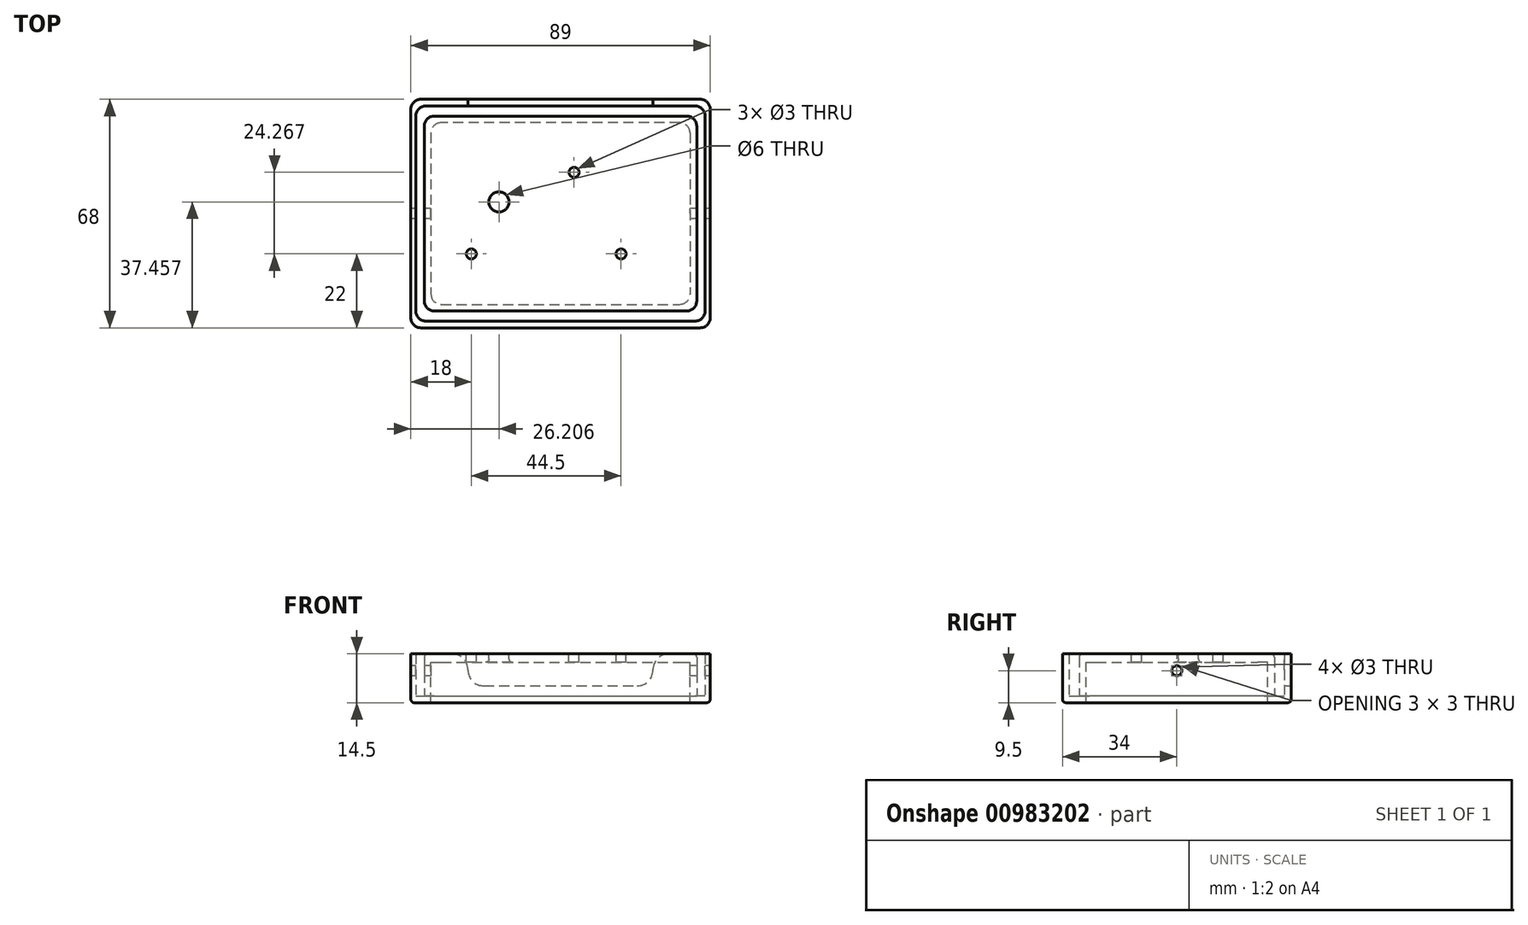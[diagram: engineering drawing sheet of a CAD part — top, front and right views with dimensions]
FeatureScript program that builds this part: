
annotation { "Feature Type Name" : "Feature", "Feature Type Description" : "" }
export const myFeature = defineFeature(function(context is Context, id is Id, definition is map)
    precondition{}
    {
        {
            var Q0;
            Q0=qCreatedBy(makeId("Top.planeOp"),FACE);
            var sketch = newSketch(context, id + "F0", { "sketchPlane" : qUnion([Q0])});
            skLineSegment(sketch, "E0.bottom", {"start": v(40.5, -29) * mm, "end": v(-40.5, -29) * mm});
            skLineSegment(sketch, "E0.top", {"start": v(40.5, 29) * mm, "end": v(-40.5, 29) * mm});
            skLineSegment(sketch, "E0.left", {"start": v(40.5, -29) * mm, "end": v(40.5, 29) * mm});
            skLineSegment(sketch, "E0.right", {"start": v(-40.5, -29) * mm, "end": v(-40.5, 29) * mm});
            skPoint(sketch, "E0.middle", {"position": v(0, 0) * mm});
            skSolve(sketch);
        }
        {
            var Q0;
            Q0 = qSketchRegion(id + "F0", true);
            extrude(context, id + "F1", {"entities" : qUnion([Q0]), "depth" : 2.5 * mm, "offsetDistance" : 25 * mm});
        }
        {
            var Q0;
            Q0=makeQuery(id+"F1.opExtrude","CAP_FACE",FACE,{"disambiguationData":[OSD([sQuery(id+"F0.wireOp",EDGE,"E0.bottom"),sQuery(id+"F0.wireOp",EDGE,"E0.top"),sQuery(id+"F0.wireOp",EDGE,"E0.left"),sQuery(id+"F0.wireOp",EDGE,"E0.right")])],"isStart":false});
            var sketch = newSketch(context, id + "F2", { "sketchPlane" : qUnion([Q0])});
            skCircle(sketch, "E1", {"center": v(-26.5, -12) * mm, "radius": 1.5 * mm});
            skCircle(sketch, "E2", {"center": v(18, -12) * mm, "radius": 1.5 * mm});
            skCircle(sketch, "E3", {"center": v(4.03, 12.27) * mm, "radius": 1.5 * mm});
            skCircle(sketch, "E4", {"center": v(-18.3, 3.46) * mm, "radius": 3 * mm});
            skSolve(sketch);
        }
        {
            var Q0;
            Q0 = qSketchRegion(id + "F2", true);
            extrude(context, id + "F3", {"entities" : qUnion([Q0]), "operationType" : NewBodyOperationType.REMOVE, "oppositeDirection" : true, "depth" : 25 * mm, "offsetDistance" : 25 * mm});
        }
        {
            var Q0;
            Q0=makeQuery(id+"F1.opExtrude","CAP_FACE",FACE,{"disambiguationData":[OSD([sQuery(id+"F0.wireOp",EDGE,"E0.bottom"),sQuery(id+"F0.wireOp",EDGE,"E0.top"),sQuery(id+"F0.wireOp",EDGE,"E0.left"),sQuery(id+"F0.wireOp",EDGE,"E0.right")])],"isStart":true});
            var sketch = newSketch(context, id + "F4", { "sketchPlane" : qUnion([Q0])});
            skLineSegment(sketch, "E5.bottom", {"start": v(-40.5, 29) * mm, "end": v(40.5, 29) * mm});
            skLineSegment(sketch, "E5.top", {"start": v(-40.5, 27) * mm, "end": v(40.5, 27) * mm});
            skLineSegment(sketch, "E5.left", {"start": v(-40.5, 29) * mm, "end": v(-40.5, 27) * mm});
            skLineSegment(sketch, "E5.right", {"start": v(40.5, 29) * mm, "end": v(40.5, 27) * mm});
            skLineSegment(sketch, "E6.bottom", {"start": v(40.5, -29) * mm, "end": v(-40.5, -29) * mm});
            skLineSegment(sketch, "E6.top", {"start": v(40.5, -27) * mm, "end": v(-40.5, -27) * mm});
            skLineSegment(sketch, "E6.left", {"start": v(40.5, -29) * mm, "end": v(40.5, -27) * mm});
            skLineSegment(sketch, "E6.right", {"start": v(-40.5, -29) * mm, "end": v(-40.5, -27) * mm});
            skLineSegment(sketch, "E7.bottom", {"start": v(-40.5, -29) * mm, "end": v(-38.5, -29) * mm});
            skLineSegment(sketch, "E7.top", {"start": v(-40.5, 29) * mm, "end": v(-38.5, 29) * mm});
            skLineSegment(sketch, "E7.left", {"start": v(-40.5, -29) * mm, "end": v(-40.5, 29) * mm});
            skLineSegment(sketch, "E7.right", {"start": v(-38.5, -29) * mm, "end": v(-38.5, 29) * mm});
            skLineSegment(sketch, "E8.bottom", {"start": v(40.5, 29) * mm, "end": v(38.5, 29) * mm});
            skLineSegment(sketch, "E8.top", {"start": v(40.5, -29) * mm, "end": v(38.5, -29) * mm});
            skLineSegment(sketch, "E8.left", {"start": v(40.5, 29) * mm, "end": v(40.5, -29) * mm});
            skLineSegment(sketch, "E8.right", {"start": v(38.5, 29) * mm, "end": v(38.5, -29) * mm});
            skSolve(sketch);
        }
        {
            var Q0;
            Q0 = qSketchRegion(id + "F4", true);
            extrude(context, id + "F5", {"entities" : qUnion([Q0]), "operationType" : NewBodyOperationType.ADD, "depth" : 12 * mm, "offsetDistance" : 25 * mm});
        }
        {
            var Q0;
            Q0=makeQuery(id+"F5.boolean.opBoolean","MERGE",FACE,{"derivedFrom":[makeQuery(id+"F1.opExtrude","SWEPT_FACE",FACE,{"disambiguationData":[OSD([sQuery(id+"F0.wireOp",EDGE,"E0.bottom")])]}),makeQuery(id+"F5.opExtrude","SWEPT_FACE",FACE,{"disambiguationData":[OSD([sQuery(id+"F4.wireOp",EDGE,"E5.bottom"),sQuery(id+"F4.wireOp",EDGE,"E7.top"),sQuery(id+"F4.wireOp",EDGE,"E8.bottom")])]})]});
            var sketch = newSketch(context, id + "F6", { "sketchPlane" : qUnion([Q0])});
            skLineSegment(sketch, "E9.bottom", {"start": v(44.5, -12) * mm, "end": v(-44.5, -12) * mm});
            skLineSegment(sketch, "E9.top", {"start": v(44.5, -10) * mm, "end": v(-44.5, -10) * mm});
            skLineSegment(sketch, "E9.left", {"start": v(44.5, -12) * mm, "end": v(44.5, -10) * mm});
            skLineSegment(sketch, "E9.right", {"start": v(-44.5, -12) * mm, "end": v(-44.5, -10) * mm});
            skPoint(sketch, "E9.middle", {"position": v(0, -11) * mm});
            skSolve(sketch);
        }
        {
            var Q0;
            Q0 = qSketchRegion(id + "F6", true);
            extrude(context, id + "F7", {"entities" : qUnion([Q0]), "operationType" : NewBodyOperationType.ADD, "depth" : 5 * mm, "offsetDistance" : 25 * mm, "hasSecondDirection" : true, "secondDirectionOppositeDirection" : true, "secondDirectionDepth" : 63 * mm});
        }
        {
            var Q0;
            Q0=makeQuery(id+"F7.boolean.opBoolean","MERGE",FACE,{"derivedFrom":[makeQuery(id+"F5.opExtrude","CAP_FACE",FACE,{"disambiguationData":[OSD([sQuery(id+"F4.wireOp",EDGE,"E5.bottom"),sQuery(id+"F4.wireOp",EDGE,"E5.top"),sQuery(id+"F4.wireOp",EDGE,"E6.bottom"),sQuery(id+"F4.wireOp",EDGE,"E6.top"),sQuery(id+"F4.wireOp",EDGE,"E7.bottom"),sQuery(id+"F4.wireOp",EDGE,"E7.top"),sQuery(id+"F4.wireOp",EDGE,"E7.left"),sQuery(id+"F4.wireOp",EDGE,"E7.right"),sQuery(id+"F4.wireOp",EDGE,"E8.bottom"),sQuery(id+"F4.wireOp",EDGE,"E8.top"),sQuery(id+"F4.wireOp",EDGE,"E8.left"),sQuery(id+"F4.wireOp",EDGE,"E8.right")])],"isStart":false}),makeQuery(id+"F7.opExtrude","SWEPT_FACE",FACE,{"disambiguationData":[OSD([sQuery(id+"F6.wireOp",EDGE,"E9.bottom")])]})]});
            var sketch = newSketch(context, id + "F8", { "sketchPlane" : qUnion([Q0])});
            skLineSegment(sketch, "E10.bottom", {"start": v(38.5, -27) * mm, "end": v(-38.5, -27) * mm});
            skLineSegment(sketch, "E10.top", {"start": v(38.5, 27) * mm, "end": v(-38.5, 27) * mm});
            skLineSegment(sketch, "E10.left", {"start": v(38.5, -27) * mm, "end": v(38.5, 27) * mm});
            skLineSegment(sketch, "E10.right", {"start": v(-38.5, -27) * mm, "end": v(-38.5, 27) * mm});
            skPoint(sketch, "E10.middle", {"position": v(0, 0) * mm});
            skSolve(sketch);
        }
        {
            var Q0;
            Q0 = qSketchRegion(id + "F8", true);
            extrude(context, id + "F9", {"entities" : qUnion([Q0]), "operationType" : NewBodyOperationType.REMOVE, "endBound" : BoundingType.UP_TO_NEXT, "oppositeDirection" : true, "depth" : 25 * mm, "offsetDistance" : 25 * mm});
        }
        {
            var Q0;
            {var subQ2=sQuery(id+"F6.wireOp",EDGE,"E9.top");Q0=makeQuery(id+"F7.boolean.opBoolean","SPLIT",FACE,{"disambiguationData":[TD([makeQuery(id+"F1.opExtrude","SWEPT_FACE",FACE,{"disambiguationData":[OSD([sQuery(id+"F0.wireOp",EDGE,"E0.bottom")])]})])],"derivedFrom":makeQuery(id+"F7.opExtrude","SWEPT_FACE",FACE,{"disambiguationData":[OSD([subQ2])]})});}
            var sketch = newSketch(context, id + "F10", { "sketchPlane" : qUnion([Q0])});
            skLineSegment(sketch, "E11.bottom", {"start": v(-44.5, -34) * mm, "end": v(44.5, -34) * mm});
            skLineSegment(sketch, "E11.top", {"start": v(-44.5, -32) * mm, "end": v(44.5, -32) * mm});
            skLineSegment(sketch, "E11.left", {"start": v(-44.5, -34) * mm, "end": v(-44.5, -32) * mm});
            skLineSegment(sketch, "E11.right", {"start": v(44.5, -34) * mm, "end": v(44.5, -32) * mm});
            skLineSegment(sketch, "E12.bottom", {"start": v(-44.5, 34) * mm, "end": v(44.5, 34) * mm});
            skLineSegment(sketch, "E12.top", {"start": v(-44.5, 32) * mm, "end": v(44.5, 32) * mm});
            skLineSegment(sketch, "E12.left", {"start": v(-44.5, 34) * mm, "end": v(-44.5, 32) * mm});
            skLineSegment(sketch, "E12.right", {"start": v(44.5, 34) * mm, "end": v(44.5, 32) * mm});
            skLineSegment(sketch, "E13.bottom", {"start": v(-44.5, 34) * mm, "end": v(-43, 34) * mm});
            skLineSegment(sketch, "E13.top", {"start": v(-44.5, -34) * mm, "end": v(-43, -34) * mm});
            skLineSegment(sketch, "E13.left", {"start": v(-44.5, 34) * mm, "end": v(-44.5, -34) * mm});
            skLineSegment(sketch, "E13.right", {"start": v(-43, 34) * mm, "end": v(-43, -34) * mm});
            skLineSegment(sketch, "E14.bottom", {"start": v(44.5, 34) * mm, "end": v(43, 34) * mm});
            skLineSegment(sketch, "E14.top", {"start": v(44.5, -34) * mm, "end": v(43, -34) * mm});
            skLineSegment(sketch, "E14.left", {"start": v(44.5, 34) * mm, "end": v(44.5, -34) * mm});
            skLineSegment(sketch, "E14.right", {"start": v(43, 34) * mm, "end": v(43, -34) * mm});
            skSolve(sketch);
        }
        {
            var Q0;
            Q0 = qSketchRegion(id + "F10", true);
            extrude(context, id + "F11", {"entities" : qUnion([Q0]), "operationType" : NewBodyOperationType.ADD, "depth" : 12.5 * mm, "offsetDistance" : 25 * mm});
        }
        {
            var Q0;
            Q0=makeQuery(id+"F11.boolean.opBoolean","MERGE",FACE,{"derivedFrom":[makeQuery(id+"F7.opExtrude","CAP_FACE",FACE,{"disambiguationData":[OSD([sQuery(id+"F6.wireOp",EDGE,"E9.bottom"),sQuery(id+"F6.wireOp",EDGE,"E9.top"),sQuery(id+"F6.wireOp",EDGE,"E9.left"),sQuery(id+"F6.wireOp",EDGE,"E9.right")])],"isStart":true}),makeQuery(id+"F11.opExtrude","SWEPT_FACE",FACE,{"disambiguationData":[OSD([sQuery(id+"F10.wireOp",EDGE,"E12.bottom"),sQuery(id+"F10.wireOp",EDGE,"E13.bottom"),sQuery(id+"F10.wireOp",EDGE,"E14.bottom")])]})]});
            var sketch = newSketch(context, id + "F12", { "sketchPlane" : qUnion([Q0])});
            skLineSegment(sketch, "E15.bottom", {"start": v(27.5, -7) * mm, "end": v(-27.5, -7) * mm});
            skLineSegment(sketch, "E15.top", {"start": v(27.5, 7) * mm, "end": v(-27.5, 7) * mm});
            skLineSegment(sketch, "E15.left", {"start": v(27.5, -7) * mm, "end": v(27.5, 7) * mm});
            skLineSegment(sketch, "E15.right", {"start": v(-27.5, -7) * mm, "end": v(-27.5, 7) * mm});
            skPoint(sketch, "E15.middle", {"position": v(0, 0) * mm});
            skSolve(sketch);
        }
        {
            var Q0;
            Q0 = qSketchRegion(id + "F12", true);
            extrude(context, id + "F13", {"entities" : qUnion([Q0]), "operationType" : NewBodyOperationType.REMOVE, "oppositeDirection" : true, "depth" : 2 * mm, "offsetDistance" : 25 * mm});
        }
        {
            var Q0;
            Q0=makeQuery(id+"F13.boolean.opBoolean","COPY",EDGE,{"derivedFrom":makeQuery(id+"F13.opExtrude","SWEPT_EDGE",EDGE,{"disambiguationData":[OSD([sQuery(id+"F12.wireOp",EDGE,"E15.bottom"),sQuery(id+"F12.wireOp",EDGE,"E15.right")])]})});
            var Q1;
            Q1=makeQuery(id+"F13.boolean.opBoolean","COPY",EDGE,{"derivedFrom":makeQuery(id+"F13.opExtrude","SWEPT_EDGE",EDGE,{"disambiguationData":[OSD([sQuery(id+"F12.wireOp",EDGE,"E15.bottom"),sQuery(id+"F12.wireOp",EDGE,"E15.left")])]})});
            var Q2;
            Q2=makeQuery(id+"F13.boolean.opBoolean","INTERSECT",EDGE,{"derivedFrom":[makeQuery(id+"F11.opExtrude","CAP_FACE",FACE,{"disambiguationData":[OSD([sQuery(id+"F10.wireOp",EDGE,"E11.bottom"),sQuery(id+"F10.wireOp",EDGE,"E11.top"),sQuery(id+"F10.wireOp",EDGE,"E12.bottom"),sQuery(id+"F10.wireOp",EDGE,"E12.top"),sQuery(id+"F10.wireOp",EDGE,"E13.bottom"),sQuery(id+"F10.wireOp",EDGE,"E13.top"),sQuery(id+"F10.wireOp",EDGE,"E13.left"),sQuery(id+"F10.wireOp",EDGE,"E13.right"),sQuery(id+"F10.wireOp",EDGE,"E14.bottom"),sQuery(id+"F10.wireOp",EDGE,"E14.top"),sQuery(id+"F10.wireOp",EDGE,"E14.left"),sQuery(id+"F10.wireOp",EDGE,"E14.right")])],"isStart":false}),makeQuery(id+"F13.opExtrude","SWEPT_FACE",FACE,{"disambiguationData":[OSD([sQuery(id+"F12.wireOp",EDGE,"E15.right")])]})]});
            var Q3;
            Q3=makeQuery(id+"F13.boolean.opBoolean","INTERSECT",EDGE,{"derivedFrom":[makeQuery(id+"F11.opExtrude","CAP_FACE",FACE,{"disambiguationData":[OSD([sQuery(id+"F10.wireOp",EDGE,"E11.bottom"),sQuery(id+"F10.wireOp",EDGE,"E11.top"),sQuery(id+"F10.wireOp",EDGE,"E12.bottom"),sQuery(id+"F10.wireOp",EDGE,"E12.top"),sQuery(id+"F10.wireOp",EDGE,"E13.bottom"),sQuery(id+"F10.wireOp",EDGE,"E13.top"),sQuery(id+"F10.wireOp",EDGE,"E13.left"),sQuery(id+"F10.wireOp",EDGE,"E13.right"),sQuery(id+"F10.wireOp",EDGE,"E14.bottom"),sQuery(id+"F10.wireOp",EDGE,"E14.top"),sQuery(id+"F10.wireOp",EDGE,"E14.left"),sQuery(id+"F10.wireOp",EDGE,"E14.right")])],"isStart":false}),makeQuery(id+"F13.opExtrude","SWEPT_FACE",FACE,{"disambiguationData":[OSD([sQuery(id+"F12.wireOp",EDGE,"E15.left")])]})]});
            fillet(context, id + "F14", {"entities" : qUnion([Q0, Q1, Q2, Q3]), "radius" : 4.7 * mm, "tangentPropagation" : true, "allowEdgeOverflow" : false});
        }
        {
            var Q0;
            Q0=makeQuery(id+"F5.boolean.opBoolean","MERGE",EDGE,{"derivedFrom":[makeQuery(id+"F1.opExtrude","SWEPT_EDGE",EDGE,{"disambiguationData":[OSD([sQuery(id+"F0.wireOp",EDGE,"E0.bottom"),sQuery(id+"F0.wireOp",EDGE,"E0.left")])]}),makeQuery(id+"F5.opExtrude","SWEPT_EDGE",EDGE,{"disambiguationData":[OSD([sQuery(id+"F4.wireOp",EDGE,"E8.bottom"),sQuery(id+"F4.wireOp",EDGE,"E8.left")])]})]});
            var Q1;
            Q1=makeQuery(id+"F5.boolean.opBoolean","MERGE",EDGE,{"derivedFrom":[makeQuery(id+"F1.opExtrude","SWEPT_EDGE",EDGE,{"disambiguationData":[OSD([sQuery(id+"F0.wireOp",EDGE,"E0.bottom"),sQuery(id+"F0.wireOp",EDGE,"E0.right")])]}),makeQuery(id+"F5.opExtrude","SWEPT_EDGE",EDGE,{"disambiguationData":[OSD([sQuery(id+"F4.wireOp",EDGE,"E7.top"),sQuery(id+"F4.wireOp",EDGE,"E7.left")])]})]});
            var Q2;
            Q2=makeQuery(id+"F5.boolean.opBoolean","MERGE",EDGE,{"derivedFrom":[makeQuery(id+"F1.opExtrude","SWEPT_EDGE",EDGE,{"disambiguationData":[OSD([sQuery(id+"F0.wireOp",EDGE,"E0.top"),sQuery(id+"F0.wireOp",EDGE,"E0.left")])]}),makeQuery(id+"F5.opExtrude","SWEPT_EDGE",EDGE,{"disambiguationData":[OSD([sQuery(id+"F4.wireOp",EDGE,"E8.top"),sQuery(id+"F4.wireOp",EDGE,"E8.left")])]})]});
            var Q3;
            Q3=makeQuery(id+"F5.boolean.opBoolean","MERGE",EDGE,{"derivedFrom":[makeQuery(id+"F1.opExtrude","SWEPT_EDGE",EDGE,{"disambiguationData":[OSD([sQuery(id+"F0.wireOp",EDGE,"E0.top"),sQuery(id+"F0.wireOp",EDGE,"E0.right")])]}),makeQuery(id+"F5.opExtrude","SWEPT_EDGE",EDGE,{"disambiguationData":[OSD([sQuery(id+"F4.wireOp",EDGE,"E7.bottom"),sQuery(id+"F4.wireOp",EDGE,"E7.left")])]})]});
            var Q4;
            {var subQ0=sQuery(id+"F4.wireOp",EDGE,"E8.right");var subQ1=sQuery(id+"F4.wireOp",EDGE,"E6.top");Q4=makeQuery(id+"F9.boolean.opBoolean","MERGE",EDGE,{"derivedFrom":[makeQuery(id+"F5.opExtrude","SWEPT_EDGE",EDGE,{"disambiguationData":[OSD([subQ1,subQ0])]})],"fromTools":[makeQuery(id+"F9.opExtrude","SWEPT_EDGE",EDGE,{"disambiguationData":[OSD([subQ1,subQ0,sQuery(id+"F6.wireOp",EDGE,"E9.top")])]})]});}
            var Q5;
            {var subQ0=sQuery(id+"F4.wireOp",EDGE,"E7.right");var subQ1=sQuery(id+"F4.wireOp",EDGE,"E6.top");Q5=makeQuery(id+"F9.boolean.opBoolean","MERGE",EDGE,{"derivedFrom":[makeQuery(id+"F5.opExtrude","SWEPT_EDGE",EDGE,{"disambiguationData":[OSD([subQ1,subQ0])]})],"fromTools":[makeQuery(id+"F9.opExtrude","SWEPT_EDGE",EDGE,{"disambiguationData":[OSD([subQ1,subQ0,sQuery(id+"F6.wireOp",EDGE,"E9.top")])]})]});}
            var Q6;
            {var subQ0=sQuery(id+"F4.wireOp",EDGE,"E7.right");var subQ1=sQuery(id+"F4.wireOp",EDGE,"E5.top");Q6=makeQuery(id+"F9.boolean.opBoolean","MERGE",EDGE,{"derivedFrom":[makeQuery(id+"F5.opExtrude","SWEPT_EDGE",EDGE,{"disambiguationData":[OSD([subQ1,subQ0])]})],"fromTools":[makeQuery(id+"F9.opExtrude","SWEPT_EDGE",EDGE,{"disambiguationData":[OSD([subQ1,subQ0,sQuery(id+"F6.wireOp",EDGE,"E9.top")])]})]});}
            var Q7;
            Q7=makeQuery(id+"F9.boolean.opBoolean","MERGE",EDGE,{"derivedFrom":[makeQuery(id+"F5.opExtrude","SWEPT_EDGE",EDGE,{"disambiguationData":[OSD([sQuery(id+"F4.wireOp",EDGE,"E5.top"),sQuery(id+"F4.wireOp",EDGE,"E8.right")])]})],"fromTools":[makeQuery(id+"F9.opExtrude","SWEPT_EDGE",EDGE,{"disambiguationData":[OSD([sQuery(id+"F8.wireOp",EDGE,"E10.top"),sQuery(id+"F8.wireOp",EDGE,"E10.left")])]})]});
            var Q8;
            Q8=makeQuery(id+"F11.boolean.opBoolean","MERGE",EDGE,{"derivedFrom":[makeQuery(id+"F7.opExtrude","CAP_EDGE",EDGE,{"disambiguationData":[OSD([sQuery(id+"F6.wireOp",EDGE,"E9.left")])],"isStart":true}),makeQuery(id+"F11.opExtrude","SWEPT_EDGE",EDGE,{"disambiguationData":[OSD([sQuery(id+"F10.wireOp",EDGE,"E14.bottom"),sQuery(id+"F10.wireOp",EDGE,"E14.left")])]})]});
            var Q9;
            Q9=makeQuery(id+"F11.boolean.opBoolean","MERGE",EDGE,{"derivedFrom":[makeQuery(id+"F7.opExtrude","CAP_EDGE",EDGE,{"disambiguationData":[OSD([sQuery(id+"F6.wireOp",EDGE,"E9.right")])],"isStart":false}),makeQuery(id+"F11.opExtrude","SWEPT_EDGE",EDGE,{"disambiguationData":[OSD([sQuery(id+"F10.wireOp",EDGE,"E13.top"),sQuery(id+"F10.wireOp",EDGE,"E13.left")])]})]});
            var Q10;
            Q10=makeQuery(id+"F11.boolean.opBoolean","MERGE",EDGE,{"derivedFrom":[makeQuery(id+"F7.opExtrude","CAP_EDGE",EDGE,{"disambiguationData":[OSD([sQuery(id+"F6.wireOp",EDGE,"E9.left")])],"isStart":false}),makeQuery(id+"F11.opExtrude","SWEPT_EDGE",EDGE,{"disambiguationData":[OSD([sQuery(id+"F10.wireOp",EDGE,"E14.top"),sQuery(id+"F10.wireOp",EDGE,"E14.left")])]})]});
            var Q11;
            Q11=makeQuery(id+"F11.boolean.opBoolean","MERGE",EDGE,{"derivedFrom":[makeQuery(id+"F7.opExtrude","CAP_EDGE",EDGE,{"disambiguationData":[OSD([sQuery(id+"F6.wireOp",EDGE,"E9.right")])],"isStart":true}),makeQuery(id+"F11.opExtrude","SWEPT_EDGE",EDGE,{"disambiguationData":[OSD([sQuery(id+"F10.wireOp",EDGE,"E13.bottom"),sQuery(id+"F10.wireOp",EDGE,"E13.left")])]})]});
            fillet(context, id + "F15", {"entities" : qUnion([Q0, Q1, Q2, Q3, Q4, Q5, Q6, Q7, Q8, Q9, Q10, Q11]), "radius" : 3 * mm, "tangentPropagation" : true, "allowEdgeOverflow" : false});
        }
        {
            var Q0;
            Q0=makeQuery(id+"F11.boolean.opBoolean","MERGE",FACE,{"derivedFrom":[makeQuery(id+"F7.opExtrude","SWEPT_FACE",FACE,{"disambiguationData":[OSD([sQuery(id+"F6.wireOp",EDGE,"E9.right")])]}),makeQuery(id+"F11.opExtrude","SWEPT_FACE",FACE,{"disambiguationData":[OSD([sQuery(id+"F10.wireOp",EDGE,"E13.left")])]})]});
            var sketch = newSketch(context, id + "F16", { "sketchPlane" : qUnion([Q0])});
            skCircle(sketch, "E16", {"center": v(0, -2.5) * mm, "radius": 1.5 * mm});
            skSolve(sketch);
        }
        {
            var Q0;
            Q0 = qSketchRegion(id + "F16", true);
            extrude(context, id + "F17", {"entities" : qUnion([Q0]), "operationType" : NewBodyOperationType.REMOVE, "endBound" : BoundingType.THROUGH_ALL, "oppositeDirection" : true, "depth" : 25 * mm, "offsetDistance" : 25 * mm});
        }
        {
            var Q0;
            Q0=makeQuery(id+"F11.opExtrude","SWEPT_EDGE",EDGE,{"disambiguationData":[OSD([sQuery(id+"F10.wireOp",EDGE,"E11.top"),sQuery(id+"F10.wireOp",EDGE,"E14.right")])]});
            var Q1;
            Q1=makeQuery(id+"F11.opExtrude","SWEPT_EDGE",EDGE,{"disambiguationData":[OSD([sQuery(id+"F10.wireOp",EDGE,"E11.top"),sQuery(id+"F10.wireOp",EDGE,"E13.right")])]});
            var Q2;
            Q2=makeQuery(id+"F11.opExtrude","SWEPT_EDGE",EDGE,{"disambiguationData":[OSD([sQuery(id+"F10.wireOp",EDGE,"E12.top"),sQuery(id+"F10.wireOp",EDGE,"E14.right")])]});
            var Q3;
            Q3=makeQuery(id+"F11.opExtrude","SWEPT_EDGE",EDGE,{"disambiguationData":[OSD([sQuery(id+"F10.wireOp",EDGE,"E12.top"),sQuery(id+"F10.wireOp",EDGE,"E13.right")])]});
            fillet(context, id + "F18", {"entities" : qUnion([Q0, Q1, Q2, Q3]), "radius" : 3 * mm, "tangentPropagation" : true, "allowEdgeOverflow" : false});
        }
        {
            var Q0;
            Q0=makeQuery(id+"F1.opExtrude","CAP_EDGE",EDGE,{"disambiguationData":[OSD([sQuery(id+"F0.wireOp",EDGE,"E0.bottom")])],"isStart":false});
            var Q1;
            Q1=makeQuery(id+"F5.opExtrude","CAP_EDGE",EDGE,{"disambiguationData":[OSD([sQuery(id+"F4.wireOp",EDGE,"E6.top")])],"isStart":true});
            var Q2;
            Q2=makeQuery(id+"F9.boolean.opBoolean","COPY",EDGE,{"derivedFrom":makeQuery(id+"F9.opExtrude","CAP_EDGE",EDGE,{"disambiguationData":[OSD([sQuery(id+"F8.wireOp",EDGE,"E10.bottom")])],"isStart":true})});
            var Q3;
            Q3=makeQuery(id+"F7.opExtrude","CAP_EDGE",EDGE,{"disambiguationData":[OSD([sQuery(id+"F6.wireOp",EDGE,"E9.bottom")])],"isStart":true});
            fillet(context, id + "F19", {"entities" : qUnion([Q0, Q1, Q2, Q3]), "radius" : 1 * mm, "tangentPropagation" : true, "allowEdgeOverflow" : false});
        }
        {
            var Q0;
            Q0=makeQuery(id+"F3.boolean.opBoolean","INTERSECT",EDGE,{"derivedFrom":[makeQuery(id+"F1.opExtrude","CAP_FACE",FACE,{"disambiguationData":[OSD([sQuery(id+"F0.wireOp",EDGE,"E0.bottom"),sQuery(id+"F0.wireOp",EDGE,"E0.top"),sQuery(id+"F0.wireOp",EDGE,"E0.left"),sQuery(id+"F0.wireOp",EDGE,"E0.right")])],"isStart":true}),makeQuery(id+"F3.opExtrude","SWEPT_FACE",FACE,{"disambiguationData":[OSD([sQuery(id+"F2.wireOp",EDGE,"E4")])]})]});
            fillet(context, id + "F20", {"entities" : qUnion([Q0]), "radius" : 1 * mm, "tangentPropagation" : true, "allowEdgeOverflow" : false});
        }
    });
